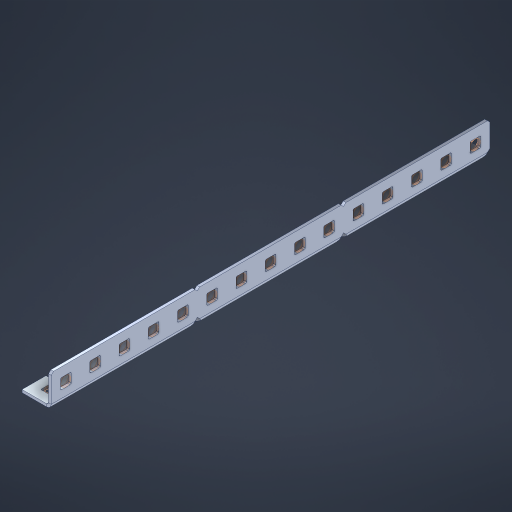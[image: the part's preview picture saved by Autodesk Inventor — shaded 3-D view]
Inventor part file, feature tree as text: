
AUTODESK INVENTOR PART (.ipt)
format: ipt  version: 2023 (Build 270158000, 158)  size: 811,520 bytes
history: native  units: in
note: dims shown in document units (in); Inventor stores cm internally (conversion verified against a paired STEP export)
features: other x52, extrude x43, sheet_metal_op x11, sketch x10, pattern_linear x2, mirror x1, chamfer x1
ambient origin geometry x8: Origin, YZ Plane, XZ Plane, XY Plane, X Axis, Y Axis, Z Axis, Center Point
bodies: Solid1 (feature_tree), Body (feature_tree)
feature tree (120):
  sheet_metal_op  "Flanges"
  other  "Flange Pattern Plane"
  other  "Flange Pattern Sketch"
  sheet_metal_op  "Flange Pattern"
  sheet_metal_op  "Body Pattern"
  pattern_linear  "Center Pattern"  Spacing1=0.0469in  [1 undecoded]
  other  "Arc Length"
  mirror  "Notch Mirror"
  pattern_linear  "Notch Pattern"  Spacing1=0.182in  [1 undecoded]
  chamfer  "End Chamfer"
  extrude  "Half Cut"  Depth=0.02in
  sketch  "Sketch1"  dims[d0=1.0in]
  other  "Plate1"
  sketch  "Sketch2"  dims[d1=7.5in]
  other  "Plate2"
  sheet_metal_op  "Bend1"
  sheet_metal_op  "Corner1"
  sketch  "Sketch3"  dims[d2=0.0469in]
  sketch  "Sketch7"  dims[d3=0.0469in]
  other  "Srf1"
  other  "Srf2"
  sketch  "Sketch8"  dims[d4=0.0234in]
  sketch  "Sketch9"  dims[d5=0.0938in]
  other  "Srf91"
  sheet_metal_op  "Body Pattern Sketch"
  other  "Srf92"
  sketch  "Sketch13"  dims[d6=0.0469in]
  sketch  "Sketch14"  dims[d7=0.5in d8=90.0deg d9=0.0312in]
  sketch  "Sketch15"  dims[d10=0.1875in]
  sketch  "Sketch16"  dims[d11=0.0469in d12=0.0469in d16=0.182in d17=0.02in d18=0.0469in d19=0.0in d20=0.25in d21=0.25in d38=5.9055in d40=0.5in d41=0.3937in d43=1.0in d46=0.172in d47=1.0in d48=0.0in d49=0.182in d50=0.02in d51=0.25in d52=0.25in d53=0.0469in d54=0.0in d55=0.172in d56=1.0in d57=0.0in d58=0.25in d60=5.9055in d62=0.5in d63=0.3937in d65=0.5in d85=0.1227in d86=0.1659in d88=0.04in d89=0.0469in d90=0.0in d91=0.04in d92=0.0491in d95=2.5in d96=0.04in d97=0.25in d98=45.0deg d99=0.25in d100=0.5in d101=0.0in d102=2.497in d106=0.182in d107=0.02in d108=0.5in d109=0.5in d110=0.0469in d111=0.0in d112=0.172in d113=0.5in d114=0.0in d117=0.5in d118=0.5in d119=0.5in]
  other  "Srf786"
  other  "Srf823"
  other  "Srf824"
  other  "Srf825"
  other  "Srf826"
  other  "Srf827"
  other  "Srf828"
  other  "Srf829"
  other  "Srf856"
  other  "Srf857"
  other  "Srf858"
  other  "Srf859"
  other  "Srf860"
  other  "Srf861"
  other  "Srf862"
  other  "Srf889"
  other  "Srf890"
  other  "Srf891"
  other  "Srf892"
  other  "Srf893"
  other  "Srf894"
  other  "Srf895"
  other  "Srf896"
  other  "Srf922"
  other  "Srf923"
  other  "Srf924"
  other  "Srf925"
  other  "Srf926"
  other  "Srf959"
  other  "Srf960"
  other  "Srf961"
  other  "Srf962"
  other  "Srf963"
  other  "Srf996"
  other  "Srf997"
  other  "Srf998"
  other  "Srf999"
  other  "Srf1000"
  other  "Srf1143"
  other  "Srf1199"
  other  "Srf1255"
  sheet_metal_op  "Flange Stamp"
  sheet_metal_op  "Flange Circle"
  sheet_metal_op  "Body Stamp"
  sheet_metal_op  "Body Circle"
  other  "Center Stamp"
  other  "Center Circle"
  sheet_metal_op  "Notch"
  extrude  "ExtrusionSrf2"  Depth=0.0469in
  extrude  "ExtrusionSrf92"  TaperAngle=0.0deg  [1 undecoded]
  extrude  "ExtrusionSrf823"  Depth=0.5in
  extrude  "ExtrusionSrf824"  Depth=0.5in
  extrude  "ExtrusionSrf825"  Depth=0.5in
  extrude  "ExtrusionSrf826"  Depth=0.5in
  extrude  "ExtrusionSrf827"  Depth=1.0in TaperAngle=0.0deg
  extrude  "ExtrusionSrf828"  Depth=0.182in
  extrude  "ExtrusionSrf829"  Depth=0.02in
  extrude  "ExtrusionSrf856"  Depth=0.5in
  extrude  "ExtrusionSrf857"  Depth=0.5in
  extrude  "ExtrusionSrf858"  Depth=0.0469in
  extrude  "ExtrusionSrf859"  TaperAngle=0.0deg  [1 undecoded]
  extrude  "ExtrusionSrf860"  Depth=0.5in
  extrude  "ExtrusionSrf861"  Depth=1.0in TaperAngle=0.0deg
  extrude  "ExtrusionSrf862"  Depth=0.5in
  extrude  "ExtrusionSrf889"  Depth=0.5in
  extrude  "ExtrusionSrf890"  Depth=0.5in
  extrude  "ExtrusionSrf891"  Depth=0.5in
  extrude  "ExtrusionSrf892"  Depth=0.5in
  extrude  "ExtrusionSrf893"  Depth=0.5in
  extrude  "ExtrusionSrf894"  Depth=0.0469in
  extrude  "ExtrusionSrf895"  TaperAngle=0.0deg  [1 undecoded]
  extrude  "ExtrusionSrf896"  Depth=0.5in
  extrude  "ExtrusionSrf922"  Depth=0.5in
  extrude  "ExtrusionSrf923"  Depth=2.5in
  extrude  "ExtrusionSrf924"  Depth=0.5in TaperAngle=45.0deg
  extrude  "ExtrusionSrf925"  Depth=0.5in
  extrude  "ExtrusionSrf926"  Depth=0.5in TaperAngle=0.0deg
  extrude  "ExtrusionSrf959"  Depth=0.5in
  extrude  "ExtrusionSrf960"  Depth=0.182in
  extrude  "ExtrusionSrf961"  Depth=0.02in
  extrude  "ExtrusionSrf962"  Depth=0.5in
  extrude  "ExtrusionSrf963"  Depth=0.5in
  extrude  "ExtrusionSrf996"  Depth=0.0469in
  extrude  "ExtrusionSrf997"  TaperAngle=0.0deg  [1 undecoded]
  extrude  "ExtrusionSrf998"  Depth=0.5in
  extrude  "ExtrusionSrf999"  Depth=0.5in TaperAngle=0.0deg
  extrude  "ExtrusionSrf1000"  Depth=0.5in
  extrude  "ExtrusionSrf1143"  Depth=0.5in
  extrude  "ExtrusionSrf1199"  Depth=0.5in
  extrude  "ExtrusionSrf1255"  [1 undecoded]
note: 7 required parameter values undecoded (feature->parameter linkage not recoverable at this tier; creation-order binding heuristic only, values carry confidence <= 0.55)
